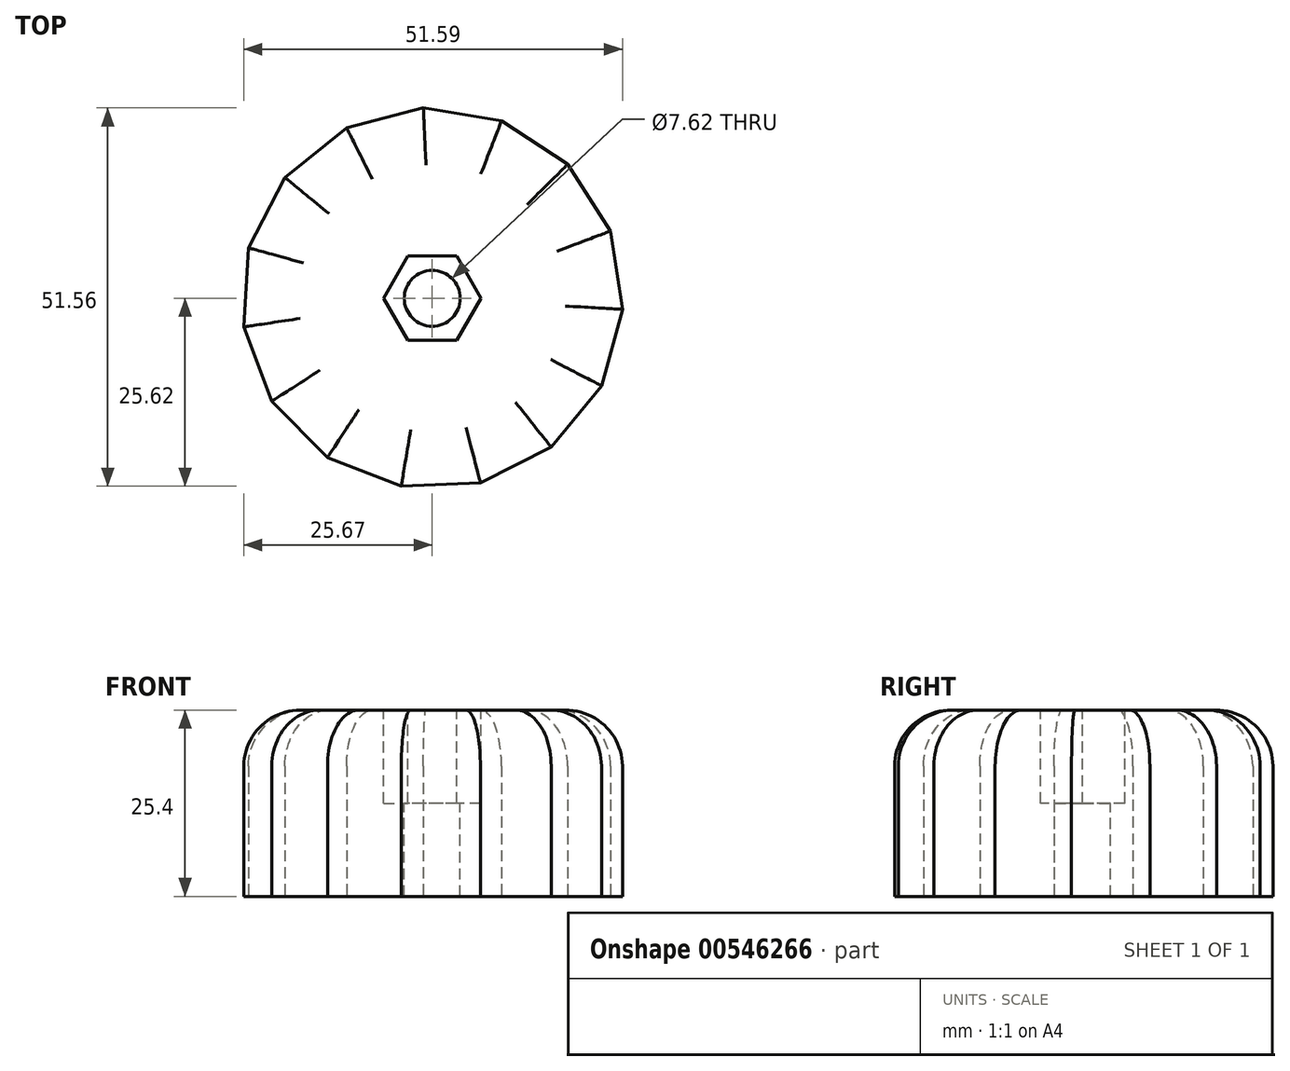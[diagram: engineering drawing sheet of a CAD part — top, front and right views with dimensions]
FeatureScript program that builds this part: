
annotation { "Feature Type Name" : "Feature", "Feature Type Description" : "" }
export const myFeature = defineFeature(function(context is Context, id is Id, definition is map)
    precondition{}
    {
        {
            var Q0;
            Q0=qCreatedBy(makeId("Top.planeOp"),FACE);
            var sketch = newSketch(context, id + "F0", { "sketchPlane" : qUnion([Q0])});
            skCircle(sketch, "E0.cCircle", {"center": v(0, 0) * mm, "radius": 25.4 * mm, "construction": true});
            skLineSegment(sketch, "E0.0", {"start": v(16.22, -20.28) * mm, "end": v(6.57, -25.12) * mm});
            skLineSegment(sketch, "E0.1", {"start": v(6.57, -25.12) * mm, "end": v(-4.21, -25.62) * mm});
            skLineSegment(sketch, "E0.2", {"start": v(-4.21, -25.62) * mm, "end": v(-14.27, -21.7) * mm});
            skLineSegment(sketch, "E0.3", {"start": v(-14.27, -21.7) * mm, "end": v(-21.86, -14.01) * mm});
            skLineSegment(sketch, "E0.4", {"start": v(-21.86, -14.01) * mm, "end": v(-25.67, -3.91) * mm});
            skLineSegment(sketch, "E0.5", {"start": v(-25.67, -3.91) * mm, "end": v(-25.04, 6.87) * mm});
            skLineSegment(sketch, "E0.6", {"start": v(-25.04, 6.87) * mm, "end": v(-20.08, 16.46) * mm});
            skLineSegment(sketch, "E0.7", {"start": v(-20.08, 16.46) * mm, "end": v(-11.65, 23.2) * mm});
            skLineSegment(sketch, "E0.8", {"start": v(-11.65, 23.2) * mm, "end": v(-1.2, 25.94) * mm});
            skLineSegment(sketch, "E0.9", {"start": v(-1.2, 25.94) * mm, "end": v(9.45, 24.19) * mm});
            skLineSegment(sketch, "E0.10", {"start": v(9.45, 24.19) * mm, "end": v(18.47, 18.25) * mm});
            skLineSegment(sketch, "E0.11", {"start": v(18.47, 18.25) * mm, "end": v(24.3, 9.16) * mm});
            skLineSegment(sketch, "E0.12", {"start": v(24.3, 9.16) * mm, "end": v(25.92, -1.51) * mm});
            skLineSegment(sketch, "E0.13", {"start": v(25.92, -1.51) * mm, "end": v(23.07, -11.93) * mm});
            skLineSegment(sketch, "E0.14", {"start": v(23.07, -11.93) * mm, "end": v(16.22, -20.28) * mm});
            skPoint(sketch, "E0.0.midPoint", {"position": v(11.4, -22.7) * mm});
            skSolve(sketch);
        }
        {
            var Q0;
            Q0=makeQuery(id+"F0.imprint","IMPRINT",FACE,{"disambiguationData":[TD([[makeQuery(id+"F0.imprint","IMPRINT",EDGE,{"derivedFrom":sQuery(id+"F0.wireOp",EDGE,"E0.0")}),-1.0]])]});
            extrude(context, id + "F1", {"entities" : qUnion([Q0]), "depth" : 25.4 * mm, "offsetDistance" : 25.4 * mm});
        }
        {
            var Q0;
            Q0=makeQuery(id+"F1.opExtrude","CAP_FACE",FACE,{"disambiguationData":[OSD([sQuery(id+"F0.wireOp",EDGE,"E0.0"),sQuery(id+"F0.wireOp",EDGE,"E0.1"),sQuery(id+"F0.wireOp",EDGE,"E0.2"),sQuery(id+"F0.wireOp",EDGE,"E0.3"),sQuery(id+"F0.wireOp",EDGE,"E0.4"),sQuery(id+"F0.wireOp",EDGE,"E0.5"),sQuery(id+"F0.wireOp",EDGE,"E0.6"),sQuery(id+"F0.wireOp",EDGE,"E0.7"),sQuery(id+"F0.wireOp",EDGE,"E0.8"),sQuery(id+"F0.wireOp",EDGE,"E0.9"),sQuery(id+"F0.wireOp",EDGE,"E0.10"),sQuery(id+"F0.wireOp",EDGE,"E0.11"),sQuery(id+"F0.wireOp",EDGE,"E0.12"),sQuery(id+"F0.wireOp",EDGE,"E0.13"),sQuery(id+"F0.wireOp",EDGE,"E0.14")])],"isStart":false});
            fillet(context, id + "F2", {"entities" : qUnion([Q0]), "radius" : 7.62 * mm, "tangentPropagation" : true, "allowEdgeOverflow" : false});
        }
        {
            var Q0;
            Q0=makeQuery(id+"F1.opExtrude","CAP_FACE",FACE,{"disambiguationData":[OSD([sQuery(id+"F0.wireOp",EDGE,"E0.0"),sQuery(id+"F0.wireOp",EDGE,"E0.1"),sQuery(id+"F0.wireOp",EDGE,"E0.2"),sQuery(id+"F0.wireOp",EDGE,"E0.3"),sQuery(id+"F0.wireOp",EDGE,"E0.4"),sQuery(id+"F0.wireOp",EDGE,"E0.5"),sQuery(id+"F0.wireOp",EDGE,"E0.6"),sQuery(id+"F0.wireOp",EDGE,"E0.7"),sQuery(id+"F0.wireOp",EDGE,"E0.8"),sQuery(id+"F0.wireOp",EDGE,"E0.9"),sQuery(id+"F0.wireOp",EDGE,"E0.10"),sQuery(id+"F0.wireOp",EDGE,"E0.11"),sQuery(id+"F0.wireOp",EDGE,"E0.12"),sQuery(id+"F0.wireOp",EDGE,"E0.13"),sQuery(id+"F0.wireOp",EDGE,"E0.14")])],"isStart":false});
            var sketch = newSketch(context, id + "F3", { "sketchPlane" : qUnion([Q0])});
            skCircle(sketch, "E1.cCircle", {"center": v(0, 0) * mm, "radius": 5.75 * mm, "construction": true});
            skLineSegment(sketch, "E1.0", {"start": v(3.32, -5.75) * mm, "end": v(-3.32, -5.75) * mm});
            skLineSegment(sketch, "E1.1", {"start": v(-3.32, -5.75) * mm, "end": v(-6.64, 0) * mm});
            skLineSegment(sketch, "E1.2", {"start": v(-6.64, 0) * mm, "end": v(-3.32, 5.75) * mm});
            skLineSegment(sketch, "E1.3", {"start": v(-3.32, 5.75) * mm, "end": v(3.32, 5.75) * mm});
            skLineSegment(sketch, "E1.4", {"start": v(3.32, 5.75) * mm, "end": v(6.64, 0) * mm});
            skLineSegment(sketch, "E1.5", {"start": v(6.64, 0) * mm, "end": v(3.32, -5.75) * mm});
            skPoint(sketch, "E1.0.midPoint", {"position": v(0, -5.75) * mm});
            skSolve(sketch);
        }
        {
            var Q0;
            Q0 = qSketchRegion(id + "F3", true);
            extrude(context, id + "F4", {"entities" : qUnion([Q0]), "operationType" : NewBodyOperationType.REMOVE, "oppositeDirection" : true, "depth" : 12.7 * mm, "offsetDistance" : 25.4 * mm});
        }
        {
            var Q0;
            Q0=makeQuery(id+"F4.boolean.opBoolean","COPY",FACE,{"derivedFrom":makeQuery(id+"F4.opExtrude","CAP_FACE",FACE,{"disambiguationData":[OSD([sQuery(id+"F3.wireOp",EDGE,"E1.0"),sQuery(id+"F3.wireOp",EDGE,"E1.1"),sQuery(id+"F3.wireOp",EDGE,"E1.2"),sQuery(id+"F3.wireOp",EDGE,"E1.3"),sQuery(id+"F3.wireOp",EDGE,"E1.4"),sQuery(id+"F3.wireOp",EDGE,"E1.5")])],"isStart":false})});
            var sketch = newSketch(context, id + "F5", { "sketchPlane" : qUnion([Q0])});
            skCircle(sketch, "E2", {"center": v(0, 0) * mm, "radius": 3.8 * mm});
            skSolve(sketch);
        }
        {
            var Q0;
            Q0 = qSketchRegion(id + "F5", true);
            extrude(context, id + "F6", {"entities" : qUnion([Q0]), "operationType" : NewBodyOperationType.REMOVE, "oppositeDirection" : true, "depth" : 25.4 * mm, "offsetDistance" : 25.4 * mm});
        }
    });
